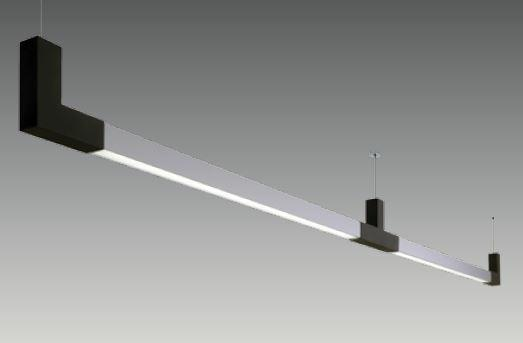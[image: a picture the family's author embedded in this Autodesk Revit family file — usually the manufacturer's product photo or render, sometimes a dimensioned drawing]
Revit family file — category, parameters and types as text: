
# Revit family: SD 3000 PLT
name_source: partatom
category: Lighting Fixtures
revit_build: Autodesk Revit 2017 (Build: 20160225_1515(x64)
units: mm (PartAtom-declared; Revit-internal decimal feet)

## family parameters
Cut with Voids When Loaded = No
Host = Face
Light Source = Yes
Part Type = Normal
Room Calculation Point = No
Round Connector Dimension = Use Diameter
Shared = No

## types (2) — shared parameters
Color Filter = 16777215
Default Elevation = 1219 mm
Dimming Lamp Color Temperature Shift = <None>
Emit Shape Visible in Rendering = Yes
Emit from Rectangle Length = 40 mm  [stored 0.131234 ft]
Emit from Rectangle Width = 1120 mm  [stored 3.67454 ft]
Light Source Symbol Size = 610 mm
Manufacturer = ARLIGHT
Type Image = SD 3000 PLT.JPG
Wattage Comments = 88W

## type names (no varying parameters)
- SDPLT.3000.88.30
- SDPLT.3000.88.40

note: [stored X ft] marks values corroborated as IEEE doubles in the binary element streams (Revit-internal decimal feet)

## geometry (parser evidence)
native form markers: Sweep x5
no freeform markers — native parametric forms only
